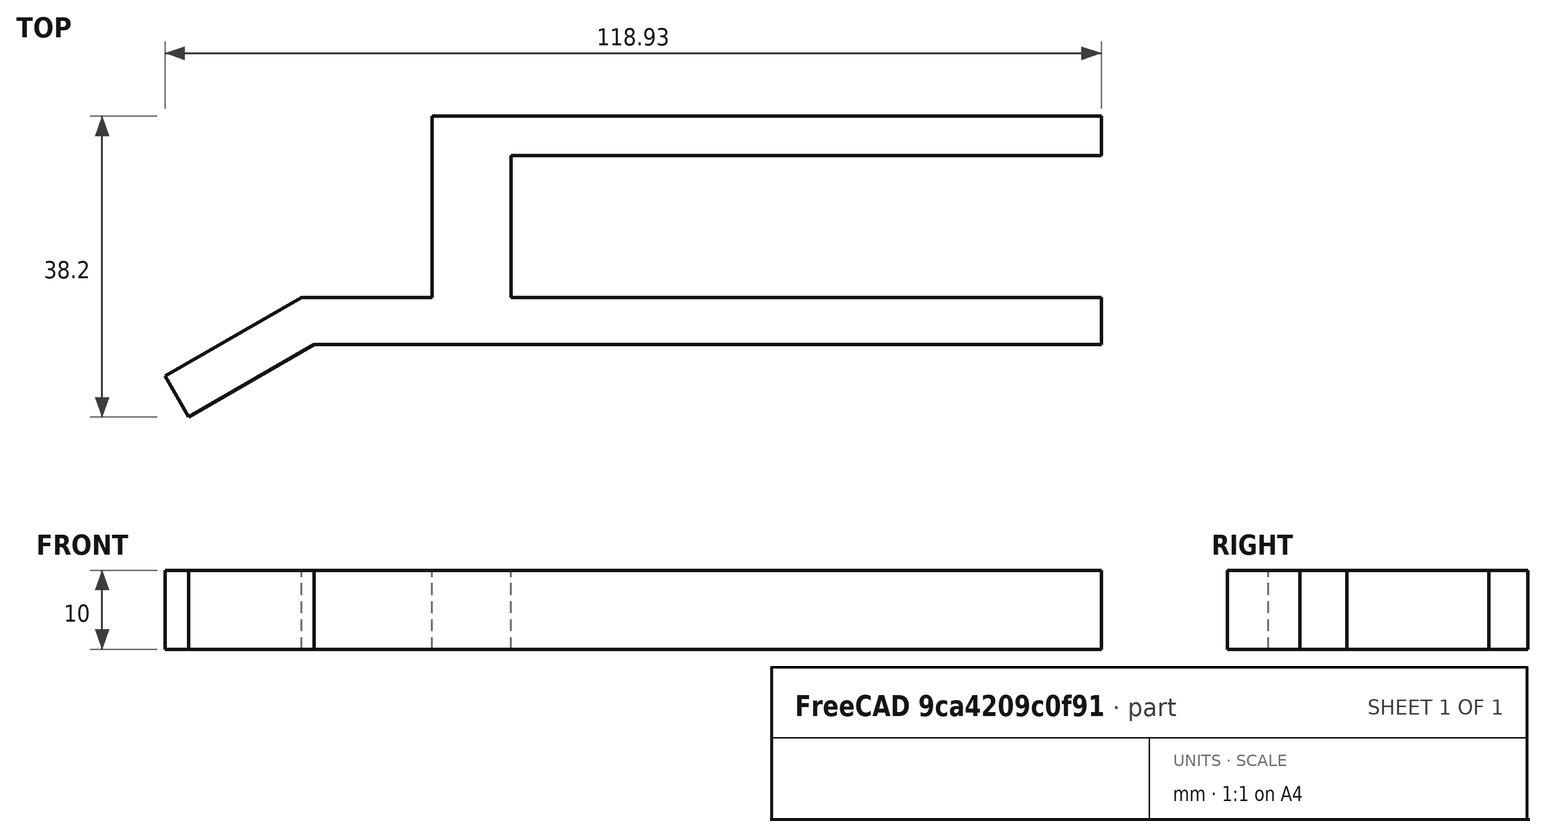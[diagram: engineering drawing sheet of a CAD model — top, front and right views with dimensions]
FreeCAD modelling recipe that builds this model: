
FCSTD DOCUMENT  (FreeCAD 0.19R)
Label: visorclip
License: All rights reserved
LicenseURL: http://en.wikipedia.org/wiki/All_rights_reserved
objects: Sketcher::SketchObject×1, PartDesign::Pad×1, PartDesign::Body×1, Mesh::Feature×1
note: 4 computed .brp shape members not serialized (recipe doc carries the construction recipe); baked Part::Feature solids carry a one-line shape summary decoded from their .brp

FEATURE [Sketcher::SketchObject] Sketch
  FullyConstrained = true
  MapMode = 5
  Support = -> [XY_Plane]
  sketch-geometry (12):
    g0: LineSegment StartX=0 StartY=0 StartZ=0 EndX=75 EndY=0 EndZ=0
    g1: LineSegment StartX=75 StartY=0 StartZ=0 EndX=75 EndY=-6 EndZ=0
    g2: LineSegment StartX=75 StartY=-6 StartZ=0 EndX=-25 EndY=-6 EndZ=0
    g3: LineSegment StartX=-10 StartY=0 StartZ=0 EndX=-10 EndY=23 EndZ=0
    g4: LineSegment StartX=-10 StartY=23 StartZ=0 EndX=75 EndY=23 EndZ=0
    g5: LineSegment StartX=75 StartY=23 StartZ=0 EndX=75 EndY=18 EndZ=0
    g6: LineSegment StartX=75 StartY=18 StartZ=0 EndX=0 EndY=18 EndZ=0
    g7: LineSegment StartX=0 StartY=18 StartZ=0 EndX=0 EndY=0 EndZ=0
    g8: LineSegment StartX=-10 StartY=0 StartZ=0 EndX=-26.6077 EndY=0 EndZ=0
    g9: LineSegment StartX=-26.6077 StartY=0 StartZ=0 EndX=-43.9282 EndY=-10 EndZ=0
    g10: LineSegment StartX=-43.9282 StartY=-10 StartZ=0 EndX=-40.9282 EndY=-15.1962 EndZ=0
    g11: LineSegment StartX=-40.9282 StartY=-15.1962 StartZ=0 EndX=-25 EndY=-6 EndZ=0
  constraints (35):
    c: Coincident(g-1,g0)
    c: PointOnObject(g0,g-1)
    c: Coincident(g0,g1)
    c: Vertical(g1)
    c: Coincident(g1,g2)
    c: Horizontal(g2)
    c: PointOnObject(g3,g-1)
    c: Vertical(g3)
    c: Coincident(g3,g4)
    c: Horizontal(g4)
    c: Coincident(g4,g5)
    c: Coincident(g5,g6)
    c: PointOnObject(g6,g-2)
    c: Horizontal(g6)
    c: Coincident(g6,g7)
    c: Coincident(g7,g0)
    c: Vertical(g5)
    c: Distance(g5) = 5
    c: Distance(g5,g0) = 18
    c: Distance(g6,g3) = 10
    c: Distance(g1) = 6
    c: DistanceX(g1) = 75
    c: DistanceX(g4) = 75
    c: Coincident(g3,g8)
    c: PointOnObject(g8,g-1)
    c: Coincident(g8,g9)
    c: Coincident(g9,g10)
    c: Coincident(g10,g11)
    c: Coincident(g2,g11)
    c: Perpendicular(g9,g10)
    c: Distance(g9) = 20
    c: Distance(g10) = 6
    c: Parallel(g9,g11)
    c: Angle(g11) = 0.523599
    c: DistanceX(g2) = -25
FEATURE [PartDesign::Pad] Pad
  Direction = (1,1,1)
  Length = 10
  Length2 = 100
  Profile = -> Sketch
  Type = 0
FEATURE [PartDesign::Body] Body
  Group = -> [Sketch,Pad]
  Origin = -> Origin
  Tip = -> Pad
FEATURE [Mesh::Feature] Mesh  label="Pad (Meshed)"
